# Revit family: IS_Archimodule_A1549_BIM_DE
name_source: partatom
category: Plumbing Fixtures
revit_build: Autodesk Revit 2015 (Build: 20140606_1530(x64)
units: mm (PartAtom-declared; Revit-internal decimal feet)

## types (1)
- A1549AA - ARCHIMODULE SOFT SHR MXR SET +HS&RAIN SH
    Accessories = www.idealspec.co.uk
    AreaUnits = millimeters
    Assembly Code = C1030200
    AssetType = Fixed
    BIMObjectName = ISI_IdealStandard_ShowerFittingsPackage_Archimodule_A1549
    BarCode = 4015413320504
    Brand = Ideal Standard
    Color = Chromium Plated
    ConnectionType = Plumbing
    Cost = 0 $
    Description = ARCHIMODULE SOFT SHR MXR SET +HS&RAIN SH
    DurationUnit = year
    Features = ARCHIMODULE SOFT SHR MXR SET +HS&RAIN SH
    Finish = Chromium Plated
    Help = www.idealstandard.de
    IfcExportAs = IfcSanitaryTerminalType
    IfcExportType = SHOWER PACK
    InstallationInstructions = www.idealstandard.de
    LinearUnits = millimeters
    MainColor = Chromium Plated
    MaintenanceInformation = www.idealstandard.de
    Manufacturer = www.idealstandard.de
    ManufacturerURL = www.idealstandard.de
    Model = A1549AA
    ModelNumber = A1549AA
    ModelReference = ARCHIMODULE SOFT SHR MXR SET +HS&RAIN SH
    Name = ShowerFittingsPackage_Archimodule_A1549_ISI
    NettWeight = 8,40 KG
    NominalDepth = 720 mm
    NominalHeight = 350 mm
    NominalLength = 720 mm
    NominalWidth = 200 mm
    ProductInformation = www.idealstandard.de
    Shape = Sculptured
    Size = 350 x 720 x 200 mm
    Space = Internal
    SpareParts = www.idealstandard.de
    TestPressure = 10 bar
    URL = www.idealstandard.de
    Uniclass2015Code = Pr_40_20_87_75
    Uniclass2015Title = Shower fittings package
    Uniclass2015Version = Products v1.1

## geometry (parser evidence)
native form markers: Blend x4
no freeform markers — native parametric forms only
